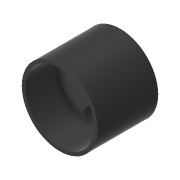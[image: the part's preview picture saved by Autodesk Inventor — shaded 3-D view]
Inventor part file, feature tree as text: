
AUTODESK INVENTOR PART (.ipt)
format: ipt  version: 2017 (Build 210142000, 142)  size: 143,872 bytes
history: native  units: in
note: dims shown in document units (in); Inventor stores cm internally (conversion verified against a paired STEP export)
features: extrude x6, sketch x5, plane x1
ambient origin geometry x8: Origin, YZ Plane, XZ Plane, XY Plane, X Axis, Y Axis, Z Axis, Center Point
bodies: Solid1 (feature_tree)
feature tree (12):
  extrude  "Extrusion1"  Depth=0.25in TaperAngle=0.0deg
  sketch  "Sketch4"  dims[d6=0.25in d11=0.0312in]
  sketch  "Sketch6"  dims[d12=0.82in d13=0.0in d14=1.0in d15=0.0in]
  plane  "Work Plane1"
  extrude  "Extrusion3"  Depth=0.25in
  extrude  "Extrusion4"  Depth=1.0in TaperAngle=0.0deg
  extrude  "Extrusion5"  Depth=0.18in
  extrude  "Extrusion6"  Depth=0.1875in
  extrude  "Extrusion7"  Depth=0.1875in
  sketch  "Sketch1"  dims[d0=0.7106in d1=0.25in d2=0.0in]
  sketch  "Sketch8"  dims[d16=0.18in d17=0.18in]
  sketch  "Sketch9"  dims[d18=0.1875in d19=0.0in d20=0.11in d21=0.11in d22=0.234in d23=0.234in d24=1.0in d25=0.0in d26=0.5in d27=0.0in]
